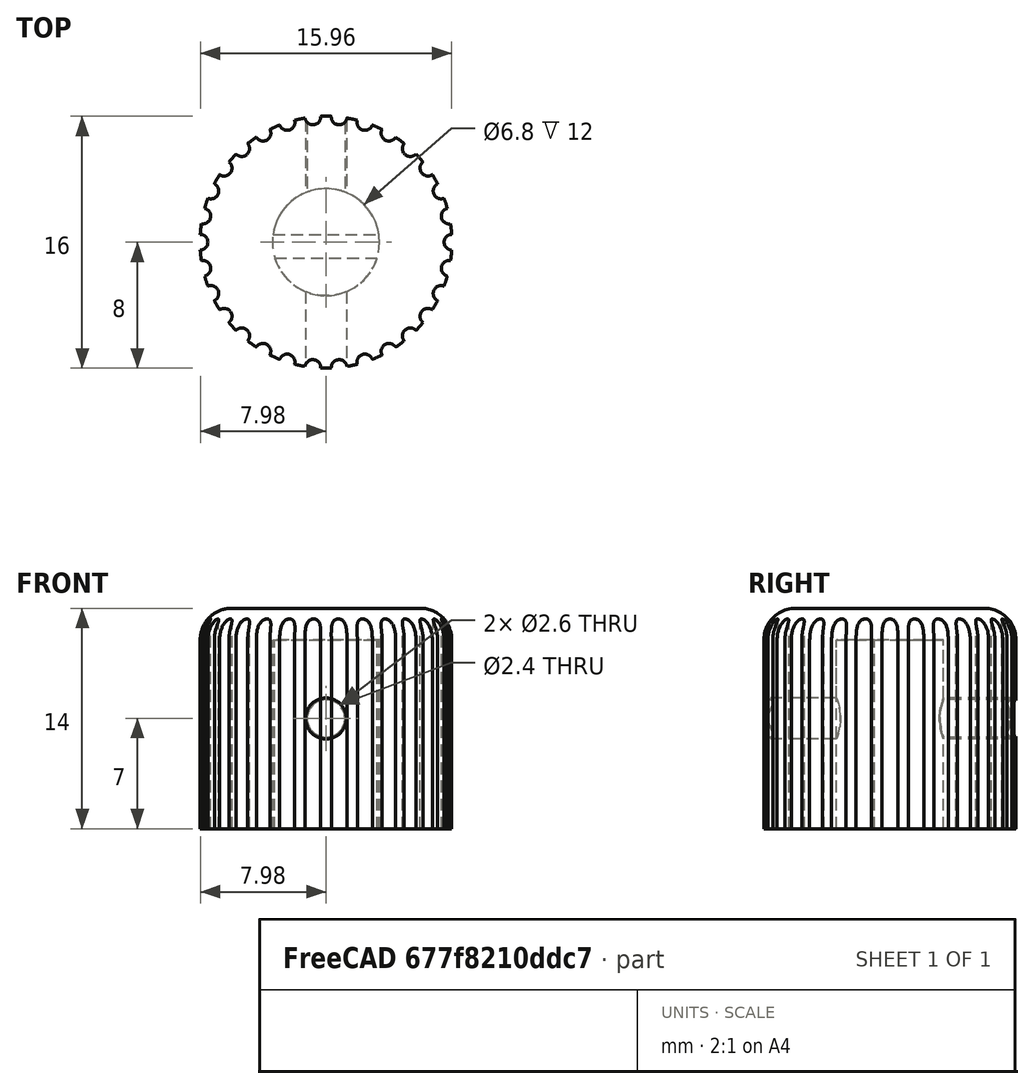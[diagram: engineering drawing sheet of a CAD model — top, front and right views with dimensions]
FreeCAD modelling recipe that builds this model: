
FCSTD DOCUMENT  (FreeCAD 0.17R13522 (Git))
Label: v6_perilla_chica
License: CreativeCommons Attribution-ShareAlike
LicenseURL: http://creativecommons.org/licenses/by-sa/4.0/
objects: Part::Cut×8, Part::Cylinder×4, Part::Feature×2, Part::Fillet×1, Part::FeaturePython×1, Part::Box×1, Part::Fuse×1
note: 18 computed .brp shape members not serialized (recipe doc carries the construction recipe); baked Part::Feature solids carry a one-line shape summary decoded from their .brp

FEATURE [Part::Cylinder] Cylinder
  Angle = 360
  AttacherType = Attacher::AttachEngine3D
  Height = 14
  Radius = 8
FEATURE [Part::Cylinder] Cylinder001  label="perfora centro"
  Angle = 360
  AttacherType = Attacher::AttachEngine3D
  Height = 13
  Placement = pos=(0,0,-1) rot=(0,0,1;0rad)
  Radius = 3.4
FEATURE [Part::Cut] Cut
  Base = -> Cylinder
  Refine = true
  Tool = -> Cylinder001
FEATURE [Part::Cylinder] Cylinder002  label="barilla borde"
  Angle = 360
  AttacherType = Attacher::AttachEngine3D
  Height = 20
  Placement = pos=(-8,0,-1) rot=(0,0,1;0rad)
  Radius = 0.5
FEATURE [Part::Fillet] Fillet
  Base = -> Cut
  Edges = 1 edges r=2: [Edge1]
FEATURE [Part::FeaturePython] Array  # Draft array (typed FeaturePython)
  Angle = 360
  ArrayType = 1
  Axis = (0,0,1)
  Base = -> Cylinder002
  Center = (0,0,0)
  Fuse = false
  IntervalAxis = (0,0,0)
  IntervalX = (1,0,0)
  IntervalY = (0,1,0)
  IntervalZ = (0,0,0)
  NumberPolar = 30
  NumberX = 2
  NumberY = 2
  NumberZ = 1
FEATURE [Part::Cut] Cut001  label="boton sin agujeros allen"
  Base = -> Fillet
  Refine = true
  Tool = -> Array
FEATURE [Part::Feature] Cylinder001005001  label="barilla perfora alen001"
  Placement = pos=(0,27,7) rot=(1,0,0;1.5708rad)
  shape: bbox 2.4 x 26 x 2.4 mm, 3 faces (baked)
FEATURE [Part::Cut] Cut002  label="old base con un agujero para allen"
  Base = -> Cut001
  Refine = true
  Tool = -> Cylinder001005001
FEATURE [Part::Cut] Cut003
  Base = -> Fillet
  Refine = true
  Tool = -> Array
FEATURE [Part::Cut] Cut004  label="perilla con un agujero allen"
  Base = -> Cut003
  Refine = true
  Tool = -> Cylinder001005001
FEATURE [Part::Cylinder] Cylinder001005002  label="barilla perforadora 2.6mm diametro"
  Angle = 360
  AttacherType = Attacher::AttachEngine3D
  Height = 20
  Placement = pos=(0,-2,7) rot=(1,0,0;1.5708rad)
  Radius = 1.3
FEATURE [Part::Cut] Cut005  label="perilla chica"
  Base = -> Cut004
  Refine = true
  Tool = -> Cylinder001005002
FEATURE [Part::Box] Box  label="Cube"
  AttacherType = Attacher::AttachEngine3D
  Height = 12
  Length = 10
  Placement = pos=(-5,-1,0) rot=(0,0,1;0rad)
  Width = 1.5
FEATURE [Part::Fuse] Fusion  label="perilla con aletas"
  Base = -> Cut005
  Refine = true
  Tool = -> Box
FEATURE [Part::Feature] Cylinder001005002001  label="barilla perforadora 2.6mm diametro001"
  Placement = pos=(0,22,7) rot=(1,0,0;1.5708rad)
  shape: bbox 2.6 x 20 x 2.6 mm, 3 faces (baked)
FEATURE [Part::Cut] Cut006
  Base = -> Fusion
  Refine = true
  Tool = -> Cylinder001005002001
FEATURE [Part::Cut] Cut007  label="perilla chica con 2 agujeros allen y aletas"
  Base = -> Cut006
  Refine = true
  Tool = -> Cylinder001005002
